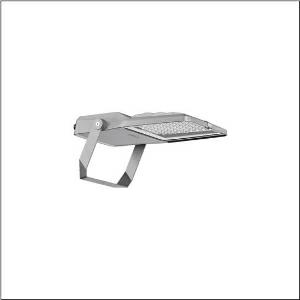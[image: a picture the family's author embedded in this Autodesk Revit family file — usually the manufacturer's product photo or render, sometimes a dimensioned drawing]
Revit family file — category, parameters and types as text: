
# Revit family: floodlight_fl_21_iq_mini___pl43_5xa7771b2a1a_26ba
name_source: partatom
category: Lighting Fixtures
units: mm (PartAtom-declared; Revit-internal decimal feet)

## family parameters
Cut with Voids When Loaded = No
Host = Face
Light Source = No
Part Type = Normal
Room Calculation Point = No
Round Connector Dimension = Use Diameter
Shared = No

## types (1)
- --- (1 x LED, 6400 lm, 45.5 W, 3000K)
    Apparent Load = 46 VA
    CIE Flux Codes = 27 78 99 100 100
    Color Rendering = 70
    Color Temperature = 3000K
    Default Elevation = 1800 mm
    Description = Floodlight FL 21 iQ mini, floodlight, primary light control with lens, of PMMA, primary optical cover: protective disc, of toughened safety glass, transparent, light distribution: PL43, light emission: direct distribution, installation type: surface-mounted, lamps: LED, High Power LED, rated values: 6.400lm | 45,5W | 140,7lm/W (begin service life); end service life: 6.400lm | 48W; at 50% lumin. flux: 3.200lm | 21,5W | 148,8lm/W, colour temperature: 3000K, colour rendering: CRI > 70, light colour: 730, light setting 1 begin service life: 100% | 6.400lm | 45,5W | 140,7lm/W | 3.000K, light setting 1 end service life: 48W, further light settings possible, control: Auto-Match, Temp-Guard, Lumen-Switch, Night-Set, Smart-Wire, Light-Fading, Desk-Remote (wireless, voltage-free reading and setting of iQ features in the workshop via application-optimized NFC function/RFID function), optimised constant luminous flux control (CLO 2.0), pre-setting: linear dimming characteristic, with terminal, 6-pole, mains connection: 220..240V, AC, 50/60Hz, luminaire housing, of diecast aluminium, powder-coated, SITECO metallic grey (DB 702S), corrosivity category C5 mid according to DIN EN ISO 12944suitable for swimming poolschlorine-resistant, sealing non-destructively replaceable, mounting bracket, of steel, galvanised, powder-coated, SITECO metallic grey (DB 702S), protection rating (complete): IP66, insulation class (complete): insulation class II (safety insulation), certification: CE, ENEC, VDE, protection symbol: D, impact resistance: IK08, permissible operating ambient temperature: -40..+40°C, permissible operating ambient temperature for outdoor applications: -40..+50°C, standard: DIN EN 12944, LABS conformity tested according to VDMA 24364:2018-05, packaging unit: 1 piece

Light Distribution: PL43
    Height = 70 mm
    Lamp = 1 x LED
    Lamp Light Flux = 6400 lm
    Lamp Power = 45.5 W
    Lamp count = 1
    Length = 485 mm
    Luminous efficacy = 141 lm/W
    Manufacturer = Siteco
    ModVariant = No
    Model = 5XA7771B2A1A
    Mounting Place = Wall
    Mounting Type = Surface mounted
    Number of Poles = 1
    OnlyDefault = Yes
    Power Factor = 1
    Product Name = Floodlight FL 21 iQ mini | PL43
    Product group = floodlight | wall mounted
    ProductGroupID = 2002
    Protection Class = Protection class II
    Protection Degree = IP 66
    RLX_Detail_Level = 1
    RLX_Emergency_Light_Flux = 0 lm
    RLX_Emergency_Type = 0
    RLX_Emergency_Type_DB = No
    RlxData = <blob elided: 96265 chars, md5=59d3c6c6>
    Socket = socket
    Standby Power = 0 W
    System Light Flux = 6400 lm
    System Power = 46 W
    Type Comments = factory setting: luminous flux: 100 % | dim-lin: 254 | 463 mA
    Type Image = l_1006845.jpg
    URL = http://relux.com
    VarID = @adj_162539
    Voltage = 0 V
    Weight = 0.00 kg
    Width = 337 mm

## geometry (parser evidence)
native form markers: Blend x4, Sweep x12
no freeform markers — native parametric forms only
